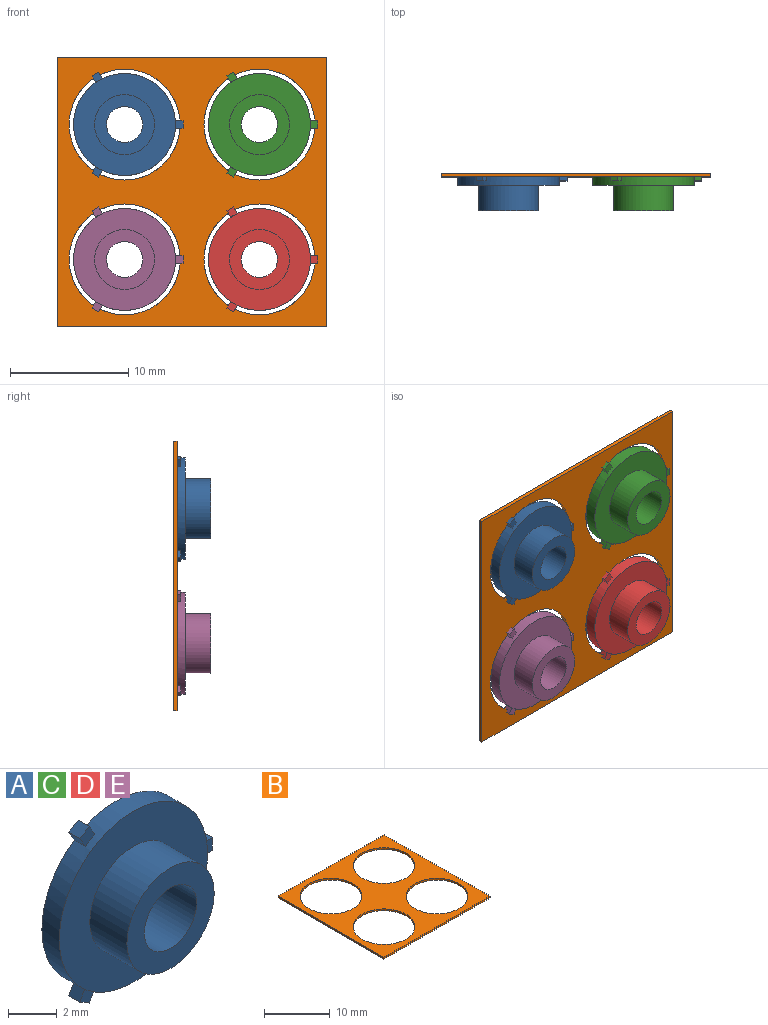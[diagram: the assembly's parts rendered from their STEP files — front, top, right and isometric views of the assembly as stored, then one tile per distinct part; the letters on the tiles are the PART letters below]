
ASSEMBLY  parts=5 mates=5
PART A: 18 faces, bbox 9.3x3.2x8.9 mm
  f0: cylinder r=4.32mm len=8.64mm, axis (0,1,0), area 26.3mm2, adj f2,f3,f6,f7,f9,f10,f11,f13
  f1: cylinder r=1.52mm len=3.18mm, axis (0,1,0), area 30.4mm2, adj f2,f5
  f2: plane 9.27x8.9mm, normal (0,1,0), area 52.5mm2, adj f0,f1,f6,f7,f8,f10,f11,f12
  f3: plane 8.64x8.64mm, normal (0,-1,0), area 38.3mm2, adj f0,f4
  f4: cylinder r=2.54mm len=5.08mm, axis (0,1,0), area 34.5mm2, adj f3,f5
  f5: plane 5.08x5.08mm, normal (0,-1,0), area 13mm2, adj f1,f4
  f6: plane 0.65x0.65mm, normal (0,0,-1), area 0.4mm2, adj f0,f2,f8,f9
  f7: plane 0.65x0.65mm, normal (0,0,1), area 0.4mm2, adj f0,f2,f8,f9
  f8: plane 0.65x0.65mm, normal (1,0,0), area 0.4mm2, adj f2,f6,f7,f9
  f9: plane 0.65x0.65mm, normal (0,-1,0), area 0.4mm2, adj f0,f6,f7,f8
  f10: plane 0.65x0.56mm, normal (-0.87,0,0.5), area 0.4mm2, adj f0,f2,f12,f13
  f11: plane 0.65x0.56mm, normal (0.87,0,-0.5), area 0.4mm2, adj f0,f2,f12,f13
  f12: plane 0.65x0.56mm, normal (-0.5,0,-0.87), area 0.4mm2, adj f2,f10,f11,f13
  f13: plane 0.88x0.88mm, normal (0,-1,0), area 0.4mm2, adj f0,f10,f11,f12
  f14: plane 0.65x0.56mm, normal (0.87,0,0.5), area 0.4mm2, adj f0,f2,f16,f17
  f15: plane 0.65x0.56mm, normal (-0.87,0,-0.5), area 0.4mm2, adj f0,f2,f16,f17
  f16: plane 0.65x0.56mm, normal (-0.5,0,0.87), area 0.4mm2, adj f2,f14,f15,f17
  f17: plane 0.88x0.88mm, normal (0,-1,0), area 0.4mm2, adj f0,f14,f15,f16
PART B: 10 faces, bbox 22.9x22.9x0.3 mm
  f0: plane 22.86x0.32mm, normal (0,-1,0), area 7.4mm2, adj f1,f3,f4,f5
  f1: plane 22.86x0.32mm, normal (1,0,0), area 7.4mm2, adj f0,f2,f4,f5
  f2: plane 22.86x0.32mm, normal (0,1,0), area 7.4mm2, adj f1,f3,f4,f5
  f3: plane 22.86x0.32mm, normal (-1,0,0), area 7.4mm2, adj f0,f2,f4,f5
  f4: plane 22.86x22.86mm, normal (0,0,1), area 245.1mm2, adj f0,f1,f2,f3,f6,f7,f8,f9
  f5: plane 22.86x22.86mm, normal (0,0,-1), area 245.1mm2, adj f0,f1,f2,f3,f6,f7,f8,f9
  f6: cylinder r=4.7mm len=9.4mm, axis (0,0,-1), area 9.5mm2, adj f4,f5
  f7: cylinder r=4.7mm len=9.4mm, axis (0,0,-1), area 9.5mm2, adj f4,f5
  f8: cylinder r=4.7mm len=9.4mm, axis (0,0,-1), area 9.5mm2, adj f4,f5
  f9: cylinder r=4.7mm len=9.4mm, axis (0,0,-1), area 9.5mm2, adj f4,f5
PART C: same geometry as A
PART D: same geometry as A
PART E: same geometry as A
PLACE A t=(16.4,0,-5.78)mm
PLACE B rot(axis=(1,0,0),90deg) t=(22.11,1.59,-11.49)mm
PLACE C t=(27.83,0,-5.78)mm
PLACE D t=(27.83,0,-17.21)mm
PLACE E t=(16.4,0,-17.21)mm
MATE cylindrical D.f0 <-> B.f8  axis (0,1,0) through (27.83,1.59,-17.21)mm
MATE cylindrical E.f0 <-> B.f9  axis (0,1,0) through (16.4,1.59,-17.21)mm
MATE parallel B.f5 <-> A.f2  axis (0,1,0) through (22.11,1.59,-11.49)mm
MATE cylindrical A.f0 <-> B.f6  axis (0,1,0) through (16.4,1.59,-5.78)mm
MATE cylindrical C.f0 <-> B.f7  axis (0,1,0) through (27.83,1.59,-5.78)mm
